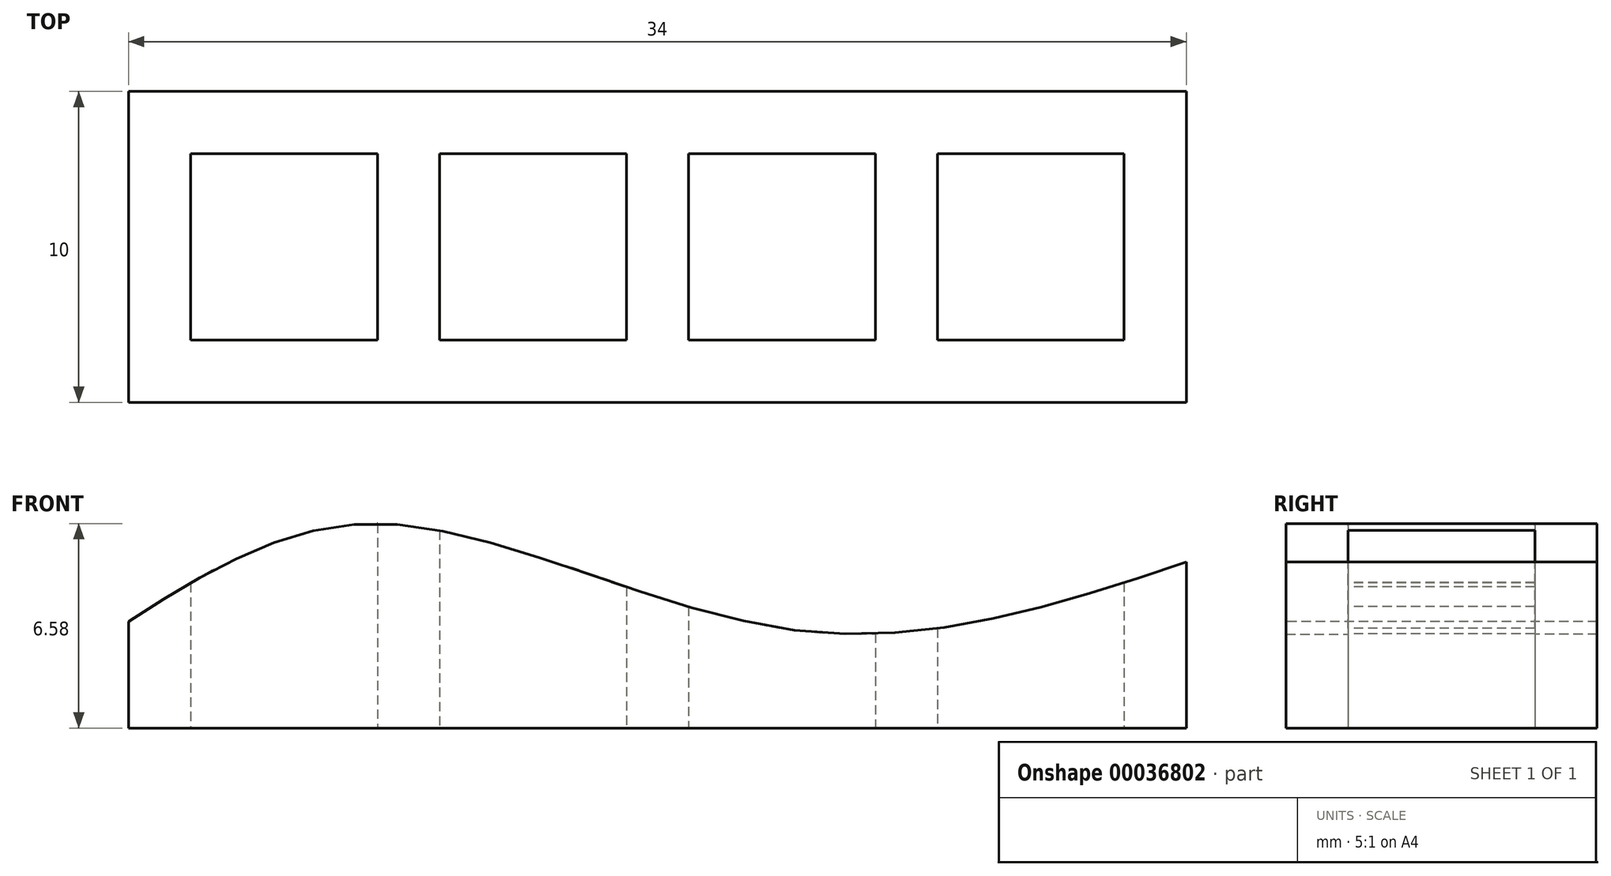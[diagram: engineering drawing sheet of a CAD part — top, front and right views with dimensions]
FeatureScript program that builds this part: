
annotation { "Feature Type Name" : "Feature", "Feature Type Description" : "" }
export const myFeature = defineFeature(function(context is Context, id is Id, definition is map)
    precondition{}
    {
        {
            var Q0;
            Q0=qCreatedBy(makeId("Top.planeOp"),FACE);
            var sketch = newSketch(context, id + "F0", { "sketchPlane" : qUnion([Q0])});
            skLineSegment(sketch, "E0.rect.bottom", {"start": v(-17, 5) * mm, "end": v(17, 5) * mm});
            skLineSegment(sketch, "E0.rect.top", {"start": v(-17, -5) * mm, "end": v(17, -5) * mm});
            skLineSegment(sketch, "E0.rect.left", {"start": v(-17, 5) * mm, "end": v(-17, -5) * mm});
            skLineSegment(sketch, "E0.rect.right", {"start": v(17, 5) * mm, "end": v(17, -5) * mm});
            skPoint(sketch, "E0.rect.middle", {"position": v(0, 0) * mm});
            skLineSegment(sketch, "E1.bottom", {"start": v(-15, 3) * mm, "end": v(-9, 3) * mm});
            skLineSegment(sketch, "E1.top", {"start": v(-15, -3) * mm, "end": v(-9, -3) * mm});
            skLineSegment(sketch, "E1.left", {"start": v(-15, 3) * mm, "end": v(-15, -3) * mm});
            skLineSegment(sketch, "E1.right", {"start": v(-9, 3) * mm, "end": v(-9, -3) * mm});
            skLineSegment(sketch, "E2.bottom", {"start": v(-7, 3) * mm, "end": v(-1, 3) * mm});
            skLineSegment(sketch, "E2.top", {"start": v(-7, -3) * mm, "end": v(-1, -3) * mm});
            skLineSegment(sketch, "E2.left", {"start": v(-7, 3) * mm, "end": v(-7, -3) * mm});
            skLineSegment(sketch, "E2.right", {"start": v(-1, 3) * mm, "end": v(-1, -3) * mm});
            skLineSegment(sketch, "E3", {"start": v(-17, 0) * mm, "end": v(17, 0) * mm, "construction": true});
            skPoint(sketch, "E4", {"position": v(-9, 0) * mm});
            skLineSegment(sketch, "E5.0.MirrorCS", {"start": v(7, 3) * mm, "end": v(1, 3) * mm});
            skLineSegment(sketch, "E6.0.MirrorCS", {"start": v(1, 3) * mm, "end": v(1, -3) * mm});
            skLineSegment(sketch, "E7.0.MirrorCS", {"start": v(7, -3) * mm, "end": v(1, -3) * mm});
            skLineSegment(sketch, "E8.0.MirrorCS", {"start": v(7, 3) * mm, "end": v(7, -3) * mm});
            skLineSegment(sketch, "E9.0.MirrorCS", {"start": v(9, 3) * mm, "end": v(9, -3) * mm});
            skLineSegment(sketch, "E10.0.MirrorCS", {"start": v(15, 3) * mm, "end": v(9, 3) * mm});
            skLineSegment(sketch, "E11.0.MirrorCS", {"start": v(15, 3) * mm, "end": v(15, -3) * mm});
            skLineSegment(sketch, "E12.0.MirrorCS", {"start": v(15, -3) * mm, "end": v(9, -3) * mm});
            skSolve(sketch);
        }
        {
            var Q0;
            Q0=qSketchRegion(id+"F0",true);
            extrude(context, id + "F1", {"entities" : qUnion([Q0]), "depth" : 8 * mm});
        }
        {
            var Q0;
            Q0=makeQuery(id+"F1.opExtrude","SWEPT_FACE",FACE,{"disambiguationData":[OSD([sQuery(id+"F0.wireOp",EDGE,"E0.rect.top")])]});
            var sketch = newSketch(context, id + "F2", { "sketchPlane" : qUnion([Q0])});
            skFitSpline(sketch, "E13", {"points": [v(-17, 3.43) * mm, v(-8.87, 6.57) * mm, v(4.28, 3.17) * mm, v(17, 5.34) * mm], "startDerivative": vector(26.16, 16.73) * mm, "endDerivative": vector(35.55, 11.83) * mm});
            skLineSegment(sketch, "E14", {"start": v(-17, 3.43) * mm, "end": v(-17, 0) * mm});
            skLineSegment(sketch, "E15", {"start": v(-17, 0) * mm, "end": v(17, 0) * mm});
            skLineSegment(sketch, "E16", {"start": v(17, 0) * mm, "end": v(17, 5.34) * mm});
            skSolve(sketch);
        }
        {
            var Q0;
            {var subQ3=sQuery(id+"F2.wireOp",EDGE,"E13");Q0=makeQuery(id+"F2.imprint","IMPRINT",FACE,{"disambiguationData":[TD([[makeQuery(id+"F2.imprint","IMPRINT",EDGE,{"derivedFrom":subQ3}),1.0]])]});}
            extrude(context, id + "F3", {"entities" : qUnion([Q0]), "operationType" : NewBodyOperationType.REMOVE, "oppositeDirection" : true, "depth" : 25 * mm});
        }
    });
